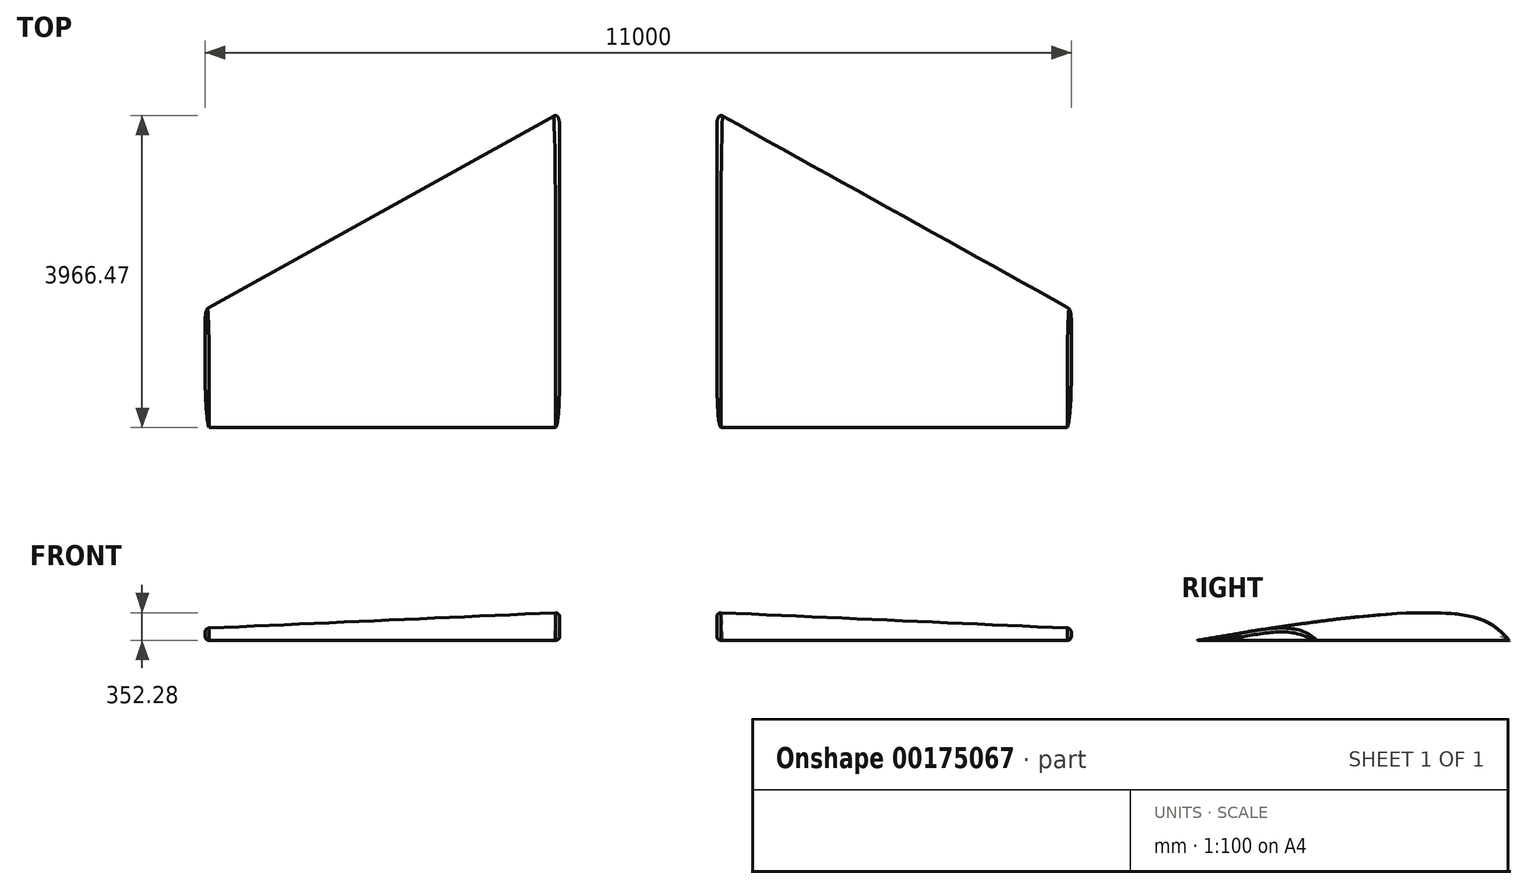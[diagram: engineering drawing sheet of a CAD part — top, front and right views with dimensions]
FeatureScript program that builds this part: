
annotation { "Feature Type Name" : "Feature", "Feature Type Description" : "" }
export const myFeature = defineFeature(function(context is Context, id is Id, definition is map)
    precondition{}
    {
        {
            var Q0;
            Q0=qCreatedBy(makeId("Right.planeOp"),FACE);
            var sketch = newSketch(context, id + "F0", { "sketchPlane" : qUnion([Q0])});
            skLineSegment(sketch, "E0", {"start": v(-2000, 0) * mm, "end": v(2000, 0) * mm});
            skFitSpline(sketch, "E1", {"points": [v(2000, 0) * mm, v(1150, 350) * mm, v(-2000, 0) * mm], "startDerivative": vector(-1838.86, 2296.85) * mm, "endDerivative": vector(-6608.78, -1143.42) * mm});
            skSolve(sketch);
        }
        {
            var Q0;
            Q0=qCreatedBy(makeId("Right.planeOp"),FACE);
            cPlane(context, id + "F1", {"entities" : qUnion([Q0]), "cplaneType" : CPlaneType.OFFSET, "offset" : 4500 * mm, "oppositeDirection" : true, "width" : 150 * mm, "height" : 150 * mm});
        }
        {
            var Q0;
            Q0=qCreatedBy(id+"F1.planeOp",FACE);
            var sketch = newSketch(context, id + "F2", { "sketchPlane" : qUnion([Q0])});
            skFitSpline(sketch, "E2", {"points": [v(-497.75, 0) * mm, v(-1997.75, 0) * mm], "startDerivative": vector(-949.58, 971.46) * mm, "endDerivative": vector(-1587.82, -146.42) * mm});
            skLineSegment(sketch, "E3", {"start": v(-497.75, 0) * mm, "end": v(-1997.75, 0) * mm});
            skSolve(sketch);
        }
        {
            var Q0;
            Q0=makeQuery(id+"F0.imprint","IMPRINT",FACE,{"disambiguationData":[TD([[makeQuery(id+"F0.imprint","IMPRINT",EDGE,{"derivedFrom":sQuery(id+"F0.wireOp",EDGE,"E0")}),1.0]])]});
            var Q1;
            Q1=makeQuery(id+"F2.imprint","IMPRINT",FACE,{"disambiguationData":[TD([[makeQuery(id+"F2.imprint","IMPRINT",EDGE,{"derivedFrom":sQuery(id+"F2.wireOp",EDGE,"E2")}),1.0]])]});
            loft(context, id + "F3", {"sheetProfilesArray" : [{ "sheetProfileEntities" : qUnion([Q0]) }, { "sheetProfileEntities" : qUnion([Q1]) }]});
        }
        {
            var Q0;
            Q0=makeQuery(id+"F3.opLoft","CAP_FACE",FACE,{"disambiguationData":[OSD([makeQuery(id+"F0.imprint","IMPRINT",FACE,{"disambiguationData":[TD([[makeQuery(id+"F0.imprint","IMPRINT",EDGE,{"derivedFrom":sQuery(id+"F0.wireOp",EDGE,"E0")}),1.0]])]})])],"isStart":true});
            var Q1;
            Q1=makeQuery(id+"F3.opLoft","CAP_FACE",FACE,{"disambiguationData":[OSD([makeQuery(id+"F2.imprint","IMPRINT",FACE,{"disambiguationData":[TD([[makeQuery(id+"F2.imprint","IMPRINT",EDGE,{"derivedFrom":sQuery(id+"F2.wireOp",EDGE,"E2")}),1.0]])]})])],"isStart":true});
            fillet(context, id + "F4", {"entities" : qUnion([Q0, Q1]), "radius" : 50 * mm, "tangentPropagation" : true, "allowEdgeOverflow" : false});
        }
        {
            var Q0;
            Q0=qCreatedBy(makeId("Right.planeOp"),FACE);
            cPlane(context, id + "F5", {"entities" : qUnion([Q0]), "cplaneType" : CPlaneType.OFFSET, "offset" : 1000 * mm, "width" : 150 * mm, "height" : 150 * mm});
        }
        {
            var Q0;
            Q0=makeQuery(id+"F3.opLoft","SWEPT_BODY",BODY,{"disambiguationData":[OSD([makeQuery(id+"F0.imprint","IMPRINT",FACE,{"disambiguationData":[TD([[makeQuery(id+"F0.imprint","IMPRINT",EDGE,{"derivedFrom":sQuery(id+"F0.wireOp",EDGE,"E0")}),1.0]])]}),makeQuery(id+"F2.imprint","IMPRINT",FACE,{"disambiguationData":[TD([[makeQuery(id+"F2.imprint","IMPRINT",EDGE,{"derivedFrom":sQuery(id+"F2.wireOp",EDGE,"E2")}),1.0]])]})])]});
            var Q1;
            Q1=qCreatedBy(id+"F5.planeOp",FACE);
            mirror(context, id + "F6", {"entities" : qUnion([Q0]), "mirrorPlane" : qUnion([Q1])});
        }
    });
